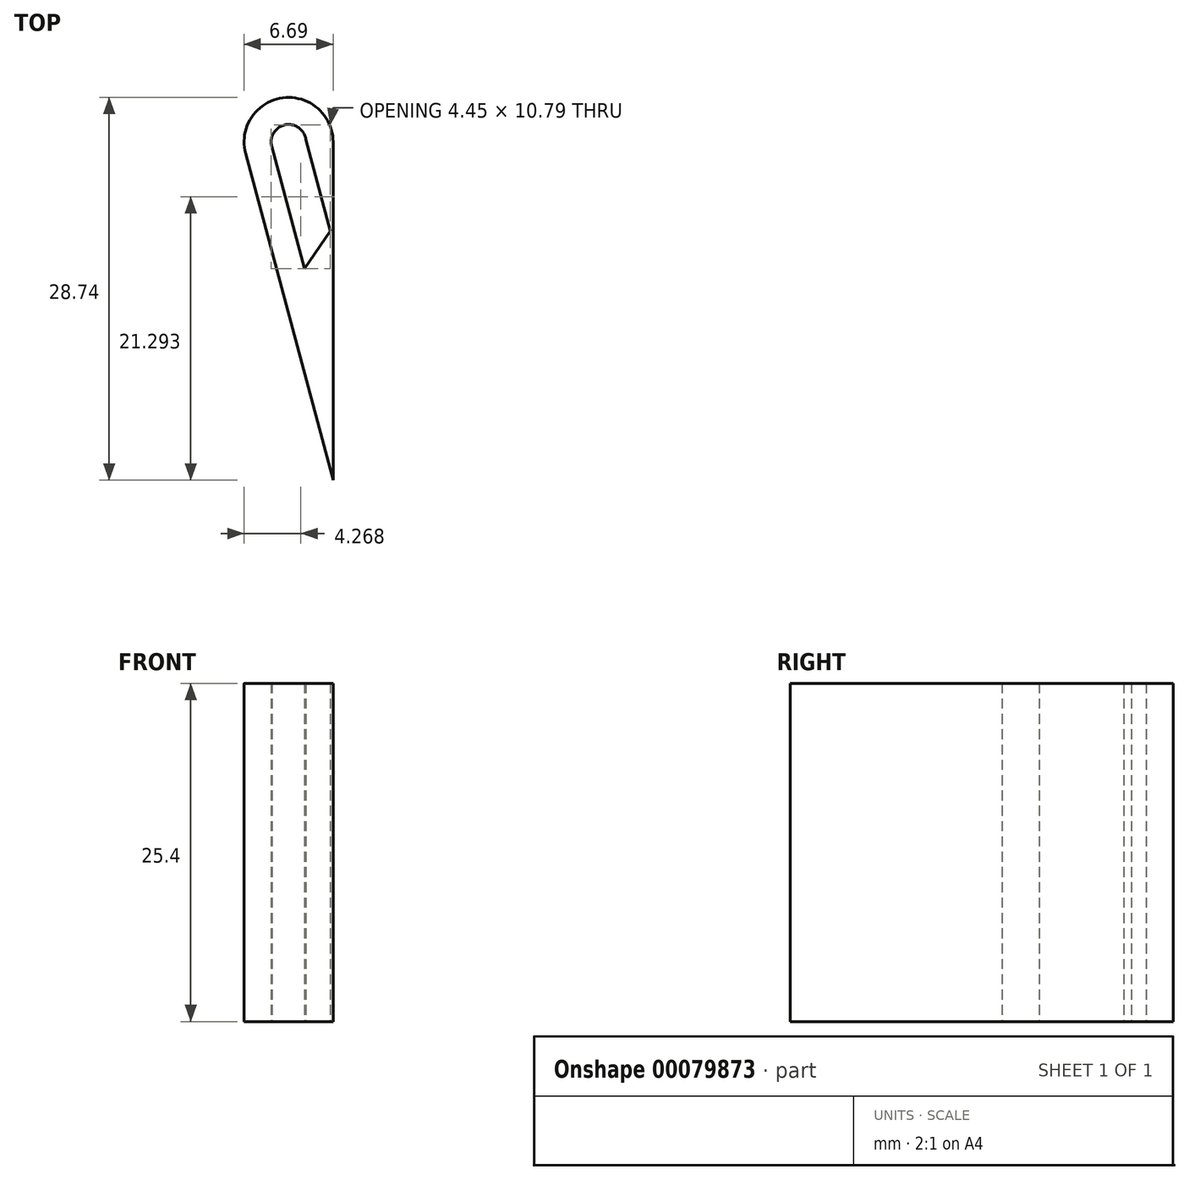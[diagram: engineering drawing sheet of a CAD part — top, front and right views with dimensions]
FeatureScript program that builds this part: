
annotation { "Feature Type Name" : "Feature", "Feature Type Description" : "" }
export const myFeature = defineFeature(function(context is Context, id is Id, definition is map)
    precondition{}
    {
        {
            var Q0;
            Q0=qCreatedBy(makeId("Top.planeOp"),FACE);
            var sketch = newSketch(context, id + "F0", { "sketchPlane" : qUnion([Q0])});
            skLineSegment(sketch, "E0", {"start": v(0, 0) * mm, "end": v(0, 25.4) * mm});
            skLineSegment(sketch, "E1", {"start": v(0, 0) * mm, "end": v(-6.57, 24.53) * mm});
            skArc(sketch, "E2", {"start": v(0, 25.4) * mm, "mid": v(-3.78, 28.72) * mm, "end": v(-6.57, 24.53) * mm});
            skArc(sketch, "E3", {"start": v(-2.05, 25.6) * mm, "mid": v(-3.63, 26.68) * mm, "end": v(-4.6, 25.02) * mm});
            skLineSegment(sketch, "E4", {"start": v(-2.05, 25.6) * mm, "end": v(-0.2, 18.7) * mm});
            skLineSegment(sketch, "E5", {"start": v(-4.62, 25.1) * mm, "end": v(-2.16, 15.9) * mm});
            skLineSegment(sketch, "E6", {"start": v(-2.16, 15.9) * mm, "end": v(-0.2, 18.7) * mm});
            skSolve(sketch);
        }
        {
            var Q0;
            Q0=makeQuery(id+"F0.imprint","IMPRINT",FACE,{"disambiguationData":[TD([[makeQuery(id+"F0.imprint","IMPRINT",EDGE,{"derivedFrom":sQuery(id+"F0.wireOp",EDGE,"E0")}),1.0]])]});
            extrude(context, id + "F1", {"entities" : qUnion([Q0]), "depth" : 25.4 * mm});
        }
    });
